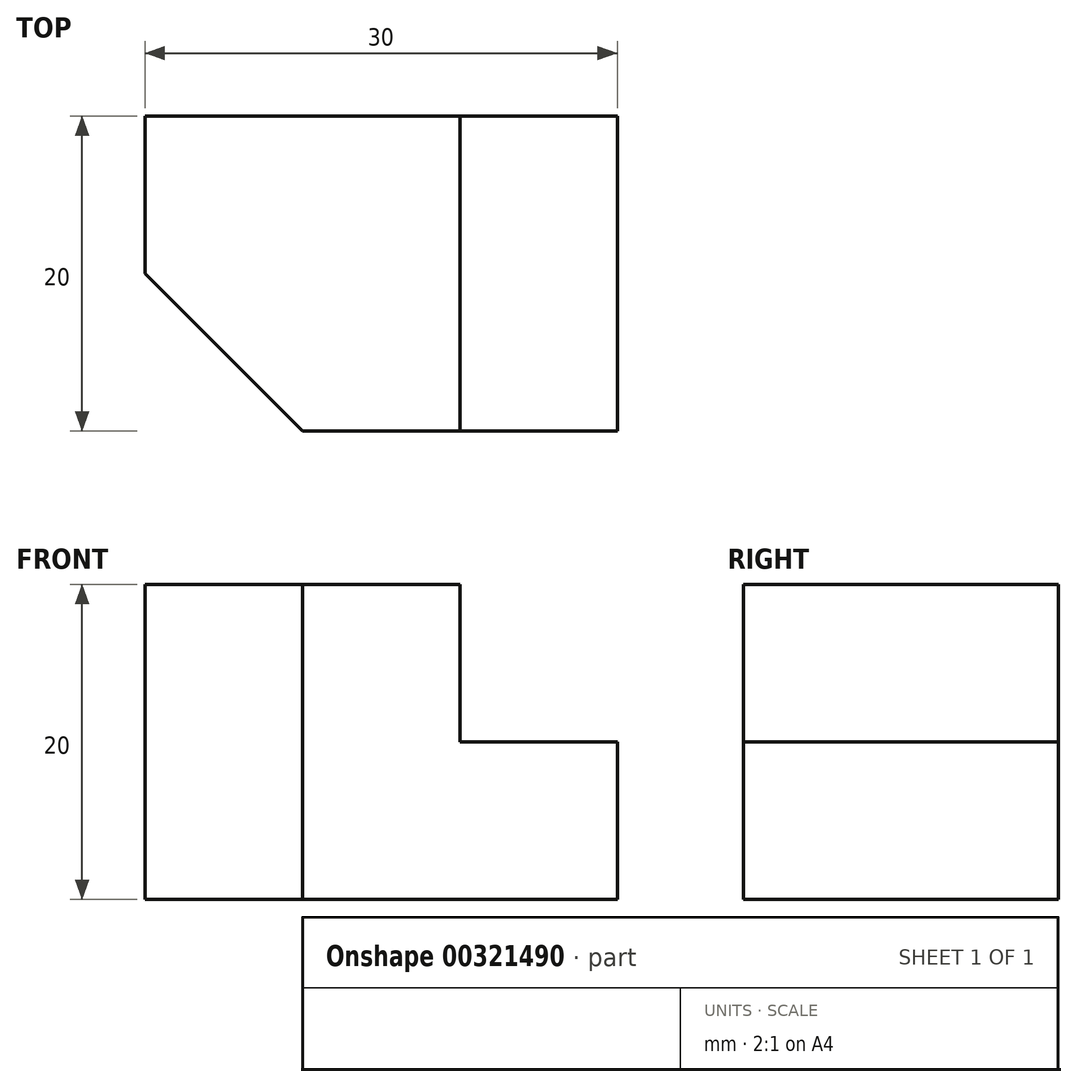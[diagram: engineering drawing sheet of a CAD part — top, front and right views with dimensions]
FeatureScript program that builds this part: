
annotation { "Feature Type Name" : "Feature", "Feature Type Description" : "" }
export const myFeature = defineFeature(function(context is Context, id is Id, definition is map)
    precondition{}
    {
        {
            var Q0;
            Q0=qCreatedBy(makeId("Front.planeOp"),FACE);
            var sketch = newSketch(context, id + "F0", { "sketchPlane" : qUnion([Q0])});
            skLineSegment(sketch, "E0", {"start": v(0, 0) * mm, "end": v(0, 20) * mm});
            skLineSegment(sketch, "E1", {"start": v(0, 0) * mm, "end": v(30, 0) * mm});
            skLineSegment(sketch, "E2", {"start": v(30, 0) * mm, "end": v(30, 10) * mm});
            skLineSegment(sketch, "E3", {"start": v(0, 20) * mm, "end": v(20, 20) * mm});
            skLineSegment(sketch, "E4", {"start": v(20, 20) * mm, "end": v(20, 10) * mm});
            skLineSegment(sketch, "E5", {"start": v(20, 10) * mm, "end": v(30, 10) * mm});
            skSolve(sketch);
        }
        {
            var Q0;
            Q0 = qSketchRegion(id + "F0", true);
            extrude(context, id + "F1", {"entities" : qUnion([Q0]), "depth" : 20 * mm});
        }
        {
            var Q0;
            Q0=makeQuery(id+"F1.opExtrude","SWEPT_FACE",FACE,{"disambiguationData":[OSD([sQuery(id+"F0.wireOp",EDGE,"E3")])]});
            var sketch = newSketch(context, id + "F2", { "sketchPlane" : qUnion([Q0])});
            skLineSegment(sketch, "E6", {"start": v(0, -10) * mm, "end": v(10, -20) * mm});
            skLineSegment(sketch, "E7", {"start": v(10, -20) * mm, "end": v(0, -20) * mm});
            skLineSegment(sketch, "E8", {"start": v(0, -20) * mm, "end": v(0, -10) * mm});
            skSolve(sketch);
        }
        {
            var Q0;
            Q0 = qSketchRegion(id + "F2", true);
            extrude(context, id + "F3", {"entities" : qUnion([Q0]), "operationType" : NewBodyOperationType.REMOVE, "endBound" : BoundingType.THROUGH_ALL, "oppositeDirection" : true, "depth" : 25 * mm});
        }
    });
